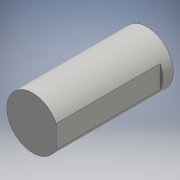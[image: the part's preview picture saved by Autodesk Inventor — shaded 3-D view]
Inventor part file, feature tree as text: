
AUTODESK INVENTOR PART (.ipt)
format: ipt  version: 2016 (Build 200138000, 138)  size: 96,768 bytes
history: native  units: mm
features: extrude x2, sketch x2, other x1
ambient origin geometry x8: Origin, YZ Plane, XZ Plane, XY Plane, X Axis, Y Axis, Z Axis, Center Point
bodies: Body1 (feature_tree)
feature tree (5):
  other  "ソリッド1"
  extrude  "押し出し1"  Depth=10.0mm
  extrude  "押し出し2"  Depth=22.0mm TaperAngle=0.0deg
  sketch  "スケッチ1"
  sketch  "スケッチ2"
